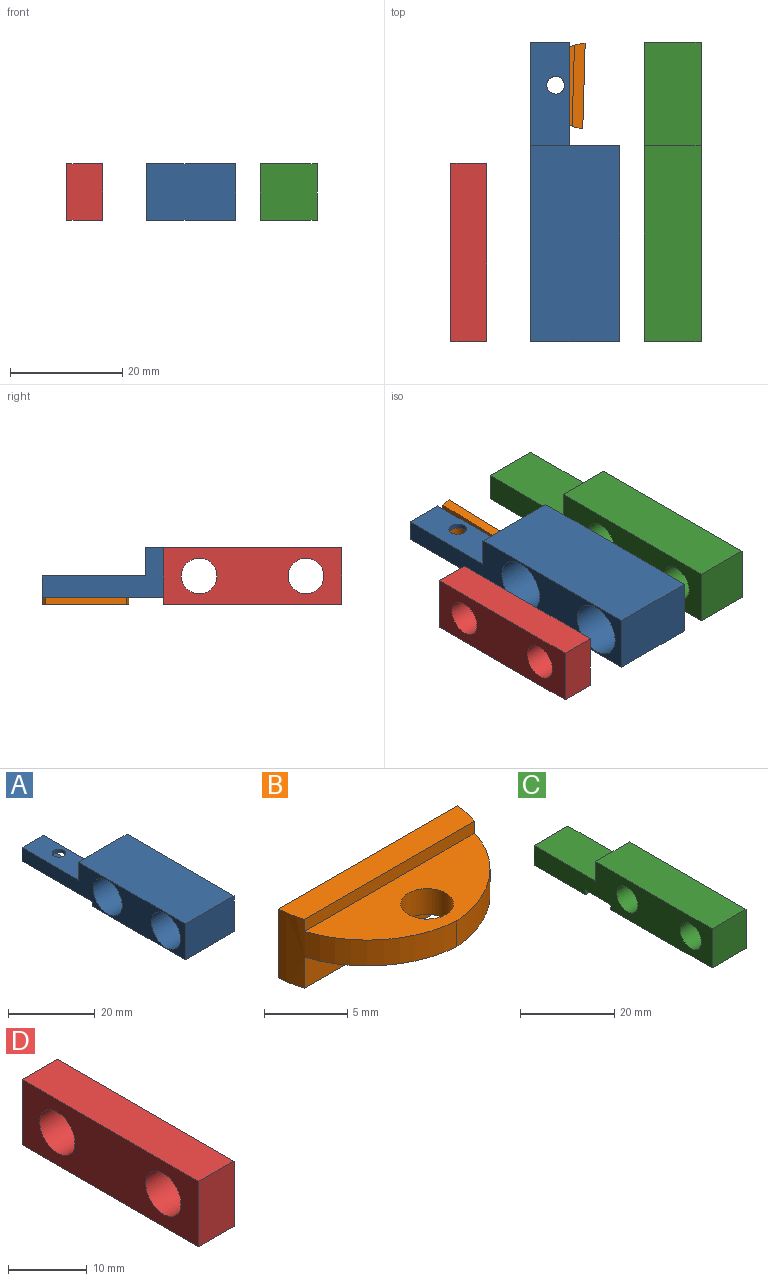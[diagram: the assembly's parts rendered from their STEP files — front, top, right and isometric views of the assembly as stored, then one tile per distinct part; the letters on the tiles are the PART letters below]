
ASSEMBLY  parts=4 mates=5
PART A: 24 faces, bbox 15.9x53.3x10.2 mm
  f0: plane 18.42x3.81mm, normal (1,0,0), area 41.8mm2, adj f3,f6,f11,f12,f19,f20,f21,f22
  f1: cylinder r=1.59mm len=3.18mm, axis (0,0,1), area 8.9mm2, adj f3,f19
  f2: plane 34.93x10.16mm, normal (1,0,0), area 285.7mm2, adj f3,f4,f5,f8,f9,f10,f11,f13
  f3: plane 22.99x15.88mm, normal (0,0,-1), area 193.3mm2, adj f0,f1,f2,f6,f7,f11,f13
  f4: cylinder r=3.17mm len=6.35mm, axis (1,0,0), area 63.3mm2, adj f2,f17
  f5: cylinder r=3.17mm len=6.35mm, axis (1,0,0), area 63.3mm2, adj f2,f15
  f6: plane 6.99x3.81mm, normal (0,1,0), area 26.6mm2, adj f0,f3,f7,f12
  f7: plane 53.34x10.16mm, normal (-1,0,0), area 276.7mm2, adj f3,f6,f8,f9,f10,f11,f12,f13
  f8: plane 34.93x15.88mm, normal (0,0,1), area 554.4mm2, adj f2,f7,f9,f11
  f9: plane 15.88x10.16mm, normal (0,-1,0), area 161.3mm2, adj f2,f7,f8,f10
  f10: plane 30.35x15.88mm, normal (0,0,-1), area 481.9mm2, adj f2,f7,f9,f13
  f11: plane 15.88x8.89mm, normal (0,1,0), area 114.5mm2, adj f0,f2,f3,f7,f8,f12
  f12: plane 18.42x6.99mm, normal (0,0,1), area 120.7mm2, adj f0,f6,f7,f11,f18
  f13: plane 15.88x1.27mm, normal (0,1,0), area 20.2mm2, adj f2,f3,f7,f10
  f14: cylinder r=4.76mm len=12.7mm, axis (-1,0,0), area 380mm2, adj f7,f15
  f15: plane 9.53x9.53mm, normal (-1,0,0), area 39.6mm2, adj f5,f14
  f16: cylinder r=4.76mm len=12.7mm, axis (-1,0,0), area 380mm2, adj f7,f17
  f17: plane 9.53x9.53mm, normal (-1,0,0), area 39.6mm2, adj f4,f16
  f18: cylinder r=1.59mm len=3.18mm, axis (0,0,1), area 8.9mm2, adj f12,f20
  f19: plane 13.97x6.35mm, normal (0,0,1), area 80.8mm2, adj f0,f1,f21,f22,f23
  f20: plane 13.97x6.35mm, normal (0,0,-1), area 80.8mm2, adj f0,f18,f21,f22,f23
  f21: plane 6.35x2.03mm, normal (0,-1,0), area 12.9mm2, adj f0,f19,f20,f23
  f22: plane 6.35x2.03mm, normal (0,1,0), area 12.9mm2, adj f0,f19,f20,f23
  f23: plane 13.97x2.03mm, normal (1,0,0), area 28.4mm2, adj f19,f20,f21,f22
PART B: 10 faces, bbox 15.2x7.6x5.1 mm
  f0: cylinder r=1.59mm len=3.18mm, axis (0,0,1), area 19mm2, adj f5,f7
  f1: plane 15.24x1.91mm, normal (0,0,1), area 28.5mm2, adj f2,f4,f8,f9
  f2: plane 15.24x5.08mm, normal (0,1,0), area 77.4mm2, adj f1,f3,f8,f9
  f3: plane 15.24x1.91mm, normal (0,0,-1), area 28.5mm2, adj f2,f6,f8,f9
  f4: plane 14.49x0.89mm, normal (0,-1,0), area 12.9mm2, adj f1,f5,f8,f9
  f5: plane 14.49x5.69mm, normal (0,0,1), area 50.9mm2, adj f0,f4,f8,f9
  f6: plane 14.49x2.29mm, normal (0,-1,0), area 33.1mm2, adj f3,f7,f8,f9
  f7: plane 14.49x5.69mm, normal (0,0,-1), area 50.9mm2, adj f0,f6,f8,f9
  f8: cylinder r=8.26mm len=7.62mm, axis (0,0,1), area 28.5mm2, adj f1,f2,f3,f4,f5,f6,f7,f9
  f9: cylinder r=8.26mm len=7.62mm, axis (0,0,1), area 28.5mm2, adj f1,f2,f3,f4,f5,f6,f7,f8
PART C: 15 faces, bbox 10.2x53.3x10.2 mm
  f0: plane 30.35x10.16mm, normal (0,0,-1), area 308.4mm2, adj f2,f3,f5,f11
  f1: plane 10.16x5.08mm, normal (0,1,0), area 41.1mm2, adj f2,f3,f6,f10,f13,f14
  f2: plane 53.34x10.16mm, normal (-1,0,0), area 375.4mm2, adj f0,f1,f4,f5,f6,f7,f8,f9
  f3: plane 53.34x10.16mm, normal (1,0,0), area 355.9mm2, adj f0,f1,f4,f5,f7,f8,f9,f10
  f4: plane 34.93x10.16mm, normal (0,0,1), area 354.8mm2, adj f2,f3,f5,f9
  f5: plane 10.16x10.16mm, normal (0,-1,0), area 103.2mm2, adj f0,f2,f3,f4
  f6: plane 15.37x1.91mm, normal (0,0,-1), area 29.3mm2, adj f1,f2,f12,f13
  f7: cylinder r=3.17mm len=10.16mm, axis (1,0,0), area 202.7mm2, adj f2,f3
  f8: cylinder r=3.17mm len=10.16mm, axis (1,0,0), area 202.7mm2, adj f2,f3
  f9: plane 10.16x5.08mm, normal (0,1,0), area 51.6mm2, adj f2,f3,f4,f10
  f10: plane 18.42x10.16mm, normal (0,0,1), area 187.1mm2, adj f1,f2,f3,f9
  f11: plane 10.16x1.27mm, normal (0,1,0), area 12.9mm2, adj f0,f2,f3,f14
  f12: plane 1.91x1.27mm, normal (0,-1,0), area 2.4mm2, adj f2,f6,f13,f14
  f13: plane 15.37x1.27mm, normal (1,0,0), area 19.5mm2, adj f1,f6,f12,f14
  f14: plane 22.99x10.16mm, normal (0,0,-1), area 204.3mm2, adj f1,f2,f3,f11,f12,f13
PART D: 8 faces, bbox 6.4x31.8x10.2 mm
  f0: plane 10.16x6.35mm, normal (0,1,0), area 64.5mm2, adj f1,f3,f4,f5
  f1: plane 31.75x10.16mm, normal (-1,0,0), area 259.2mm2, adj f0,f2,f4,f5,f6,f7
  f2: plane 10.16x6.35mm, normal (0,-1,0), area 64.5mm2, adj f1,f3,f4,f5
  f3: plane 31.75x10.16mm, normal (1,0,0), area 259.2mm2, adj f0,f2,f4,f5,f6,f7
  f4: plane 31.75x6.35mm, normal (0,0,1), area 201.6mm2, adj f0,f1,f2,f3
  f5: plane 31.75x6.35mm, normal (0,0,-1), area 201.6mm2, adj f0,f1,f2,f3
  f6: cylinder r=3.17mm len=6.35mm, axis (1,0,0), area 126.7mm2, adj f1,f3
  f7: cylinder r=3.17mm len=6.35mm, axis (1,0,0), area 126.7mm2, adj f1,f3
PLACE A rot(axis=(0,0,1),0deg) t=(-3.7,-3.62,33.37)mm
PLACE B rot(axis=(0,0,-1),91.6deg) t=(-6.05,23.07,28.29)mm
PLACE C rot(axis=(0,0,1),0deg) t=(13.7,-3.62,33.37)mm fixed
PLACE D t=(-22.67,-14.41,33.37)mm
MATE cylindrical D.f6 <-> C.f7  axis (-1,0,0) through (-25.85,-4.89,33.37)mm
MATE slider A.f14 <-> C.f8  axis (1,0,0) through (4.24,-23.94,33.37)mm
MATE cylindrical A.f1 <-> B.f0  axis (0,0,-1) through (-7.19,15.43,32.48)mm
MATE slider A.f16 <-> C.f7  axis (1,0,0) through (4.24,-4.89,33.37)mm
MATE planar A.f20 <-> B.f5  axis (0,0,-1) through (-7.89,14.74,32.48)mm
